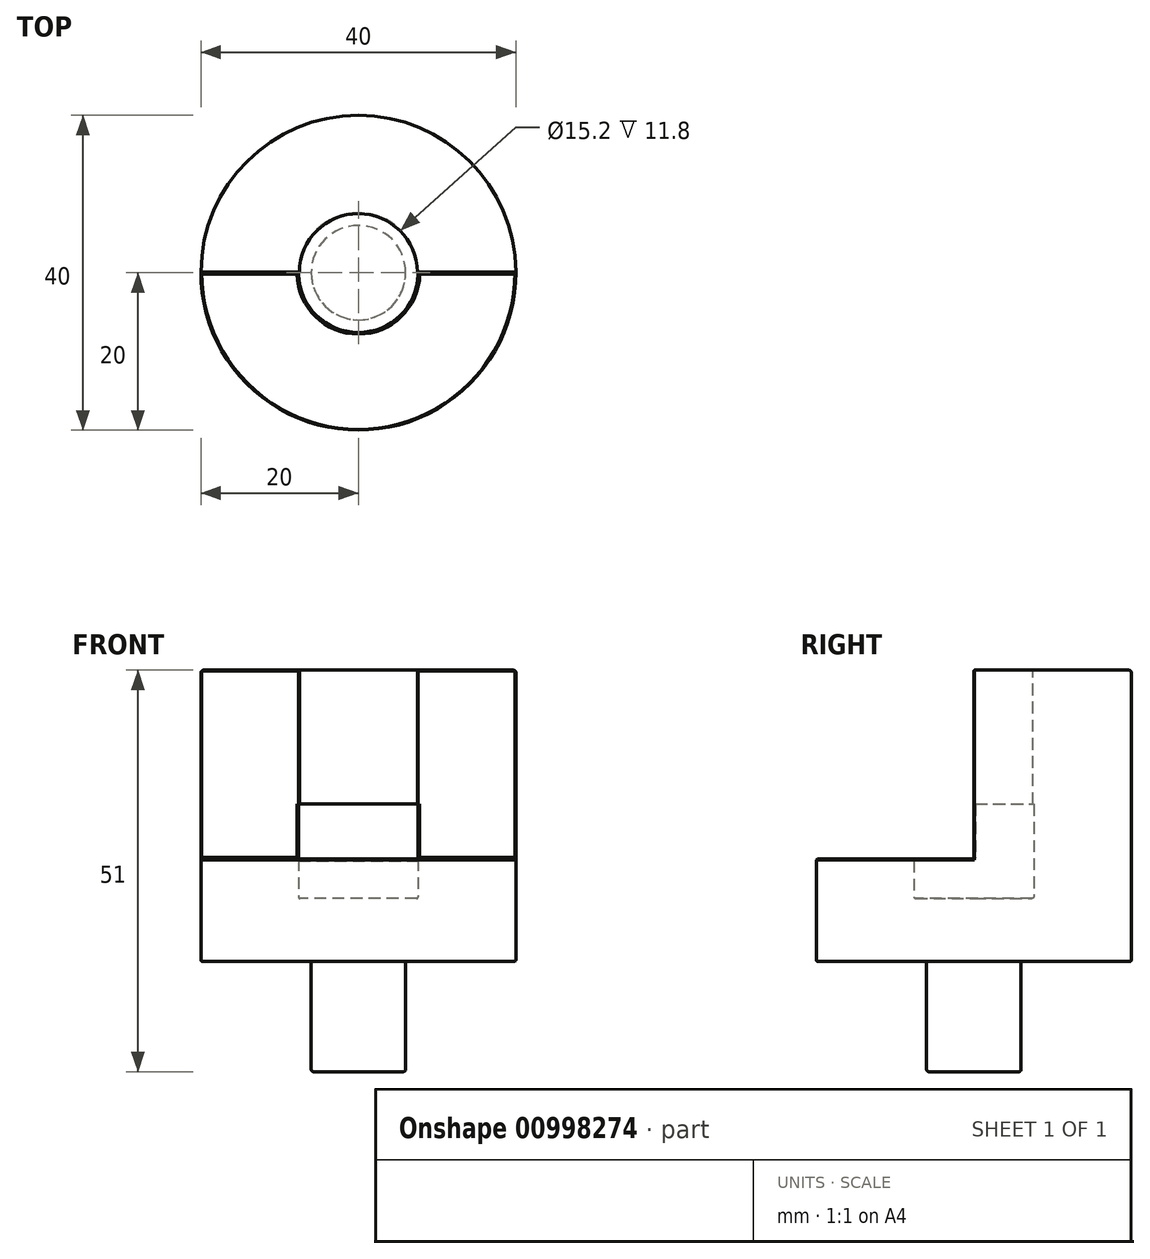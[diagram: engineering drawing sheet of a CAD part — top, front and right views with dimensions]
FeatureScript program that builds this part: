
annotation { "Feature Type Name" : "Feature", "Feature Type Description" : "" }
export const myFeature = defineFeature(function(context is Context, id is Id, definition is map)
    precondition{}
    {
        {
            var Q0;
            Q0=qCreatedBy(makeId("Top.planeOp"),FACE);
            var sketch = newSketch(context, id + "F0", { "sketchPlane" : qUnion([Q0])});
            skCircle(sketch, "E0", {"center": v(0, 0) * mm, "radius": 20 * mm});
            skSolve(sketch);
        }
        {
            var Q0;
            Q0 = qSketchRegion(id + "F0", true);
            extrude(context, id + "F1", {"entities" : qUnion([Q0]), "depth" : 37 * mm, "offsetDistance" : 25 * mm});
        }
        {
            var Q0;
            Q0=makeQuery(id+"F1.opExtrude","CAP_FACE",FACE,{"disambiguationData":[OSD([sQuery(id+"F0.wireOp",EDGE,"E0")])],"isStart":true});
            var sketch = newSketch(context, id + "F2", { "sketchPlane" : qUnion([Q0])});
            skCircle(sketch, "E1", {"center": v(0, 0) * mm, "radius": 6 * mm});
            skSolve(sketch);
        }
        {
            var Q0;
            Q0 = qSketchRegion(id + "F2", true);
            extrude(context, id + "F3", {"entities" : qUnion([Q0]), "operationType" : NewBodyOperationType.ADD, "depth" : 14 * mm, "offsetDistance" : 25 * mm});
        }
        {
            var Q0;
            Q0=makeQuery(id+"F1.opExtrude","CAP_FACE",FACE,{"disambiguationData":[OSD([sQuery(id+"F0.wireOp",EDGE,"E0")])],"isStart":false});
            var sketch = newSketch(context, id + "F4", { "sketchPlane" : qUnion([Q0])});
            skCircle(sketch, "E2", {"center": v(0, 0) * mm, "radius": 7.5 * mm});
            skSolve(sketch);
        }
        {
            var Q0;
            Q0=makeQuery(id+"F4.imprint","IMPRINT",FACE,{"disambiguationData":[TD([[makeQuery(id+"F4.imprint","IMPRINT",EDGE,{"derivedFrom":sQuery(id+"F4.wireOp",EDGE,"E2")}),1.0]])]});
            extrude(context, id + "F5", {"entities" : qUnion([Q0]), "operationType" : NewBodyOperationType.REMOVE, "oppositeDirection" : true, "depth" : 29 * mm, "offsetDistance" : 25 * mm});
        }
        {
            var Q0;
            Q0=qCreatedBy(makeId("Front.planeOp"),FACE);
            var sketch = newSketch(context, id + "F6", { "sketchPlane" : qUnion([Q0])});
            skLineSegment(sketch, "E3", {"start": v(-39.79, 13) * mm, "end": v(43.41, 13) * mm});
            skLineSegment(sketch, "E4", {"start": v(43.41, 13) * mm, "end": v(43.41, 53.9) * mm});
            skLineSegment(sketch, "E5", {"start": v(43.41, 53.9) * mm, "end": v(-42.56, 53.9) * mm});
            skLineSegment(sketch, "E6", {"start": v(-42.56, 53.9) * mm, "end": v(-39.79, 13) * mm});
            skSolve(sketch);
        }
        {
            var Q0;
            Q0=makeQuery(id+"F6.imprint","IMPRINT",FACE,{"disambiguationData":[TD([[makeQuery(id+"F6.imprint","IMPRINT",EDGE,{"derivedFrom":sQuery(id+"F6.wireOp",EDGE,"E3")}),1.0]])]});
            extrude(context, id + "F7", {"entities" : qUnion([Q0]), "operationType" : NewBodyOperationType.REMOVE, "oppositeDirection" : true, "depth" : -25 * mm, "offsetDistance" : 25 * mm});
        }
        {
            var Q0;
            Q0=makeQuery(id+"F5.boolean.opBoolean","COPY",FACE,{"derivedFrom":makeQuery(id+"F5.opExtrude","CAP_FACE",FACE,{"disambiguationData":[OSD([sQuery(id+"F4.wireOp",EDGE,"E2")])],"isStart":false})});
            var sketch = newSketch(context, id + "F8", { "sketchPlane" : qUnion([Q0])});
            skCircle(sketch, "E7", {"center": v(0, 0) * mm, "radius": 7.6 * mm});
            skSolve(sketch);
        }
        {
            var Q0;
            Q0 = qSketchRegion(id + "F8", true);
            extrude(context, id + "F9", {"entities" : qUnion([Q0]), "operationType" : NewBodyOperationType.REMOVE, "oppositeDirection" : true, "depth" : -12 * mm, "offsetDistance" : 25 * mm});
        }
        {
            var Q0;
            Q0=makeQuery(id+"F3.opExtrude","CAP_EDGE",EDGE,{"disambiguationData":[OSD([sQuery(id+"F2.wireOp",EDGE,"E1")])],"isStart":false});
            var Q1;
            Q1=makeQuery(id+"F1.opExtrude","CAP_EDGE",EDGE,{"disambiguationData":[OSD([sQuery(id+"F0.wireOp",EDGE,"E0")])],"isStart":false});
            fillet(context, id + "F10", {"entities" : qUnion([Q0, Q1]), "radius" : .3 * mm, "tangentPropagation" : true, "allowEdgeOverflow" : false});
        }
        {
            var Q0;
            Q0=makeQuery(id+"F7.boolean.opBoolean","INTERSECT",EDGE,{"disambiguationData":[OD(0.0)],"derivedFrom":[makeQuery(id+"F5.boolean.opBoolean","COPY",FACE,{"derivedFrom":makeQuery(id+"F5.opExtrude","SWEPT_FACE",FACE,{"disambiguationData":[OSD([sQuery(id+"F4.wireOp",EDGE,"E2")])]})}),makeQuery(id+"F7.opExtrude","CAP_FACE",FACE,{"disambiguationData":[OSD([sQuery(id+"F6.wireOp",EDGE,"E3"),sQuery(id+"F6.wireOp",EDGE,"E4"),sQuery(id+"F6.wireOp",EDGE,"E5"),sQuery(id+"F6.wireOp",EDGE,"E6")])],"isStart":true})]});
            var Q1;
            Q1=makeQuery(id+"F7.boolean.opBoolean","INTERSECT",EDGE,{"disambiguationData":[OD(1.0)],"derivedFrom":[makeQuery(id+"F5.boolean.opBoolean","COPY",FACE,{"derivedFrom":makeQuery(id+"F5.opExtrude","SWEPT_FACE",FACE,{"disambiguationData":[OSD([sQuery(id+"F4.wireOp",EDGE,"E2")])]})}),makeQuery(id+"F7.opExtrude","CAP_FACE",FACE,{"disambiguationData":[OSD([sQuery(id+"F6.wireOp",EDGE,"E3"),sQuery(id+"F6.wireOp",EDGE,"E4"),sQuery(id+"F6.wireOp",EDGE,"E5"),sQuery(id+"F6.wireOp",EDGE,"E6")])],"isStart":true})]});
            var Q2;
            Q2=makeQuery(id+"F5.boolean.opBoolean","COPY",EDGE,{"derivedFrom":makeQuery(id+"F5.opExtrude","CAP_EDGE",EDGE,{"disambiguationData":[OSD([sQuery(id+"F4.wireOp",EDGE,"E2")])],"isStart":true})});
            var Q3;
            Q3=makeQuery(id+"F7.boolean.opBoolean","INTERSECT",EDGE,{"disambiguationData":[OD(1.0)],"derivedFrom":[makeQuery(id+"F1.opExtrude","CAP_FACE",FACE,{"disambiguationData":[OSD([sQuery(id+"F0.wireOp",EDGE,"E0")])],"isStart":false}),makeQuery(id+"F7.opExtrude","CAP_FACE",FACE,{"disambiguationData":[OSD([sQuery(id+"F6.wireOp",EDGE,"E3"),sQuery(id+"F6.wireOp",EDGE,"E4"),sQuery(id+"F6.wireOp",EDGE,"E5"),sQuery(id+"F6.wireOp",EDGE,"E6")])],"isStart":true})]});
            var Q4;
            Q4=makeQuery(id+"F7.boolean.opBoolean","INTERSECT",EDGE,{"derivedFrom":[makeQuery(id+"F1.opExtrude","SWEPT_FACE",FACE,{"disambiguationData":[OSD([sQuery(id+"F0.wireOp",EDGE,"E0")])]}),makeQuery(id+"F7.opExtrude","SWEPT_FACE",FACE,{"disambiguationData":[OSD([sQuery(id+"F6.wireOp",EDGE,"E3")])]})]});
            var Q5;
            Q5=makeQuery(id+"F7.boolean.opBoolean","INTERSECT",EDGE,{"disambiguationData":[OD(0.0)],"derivedFrom":[makeQuery(id+"F1.opExtrude","CAP_FACE",FACE,{"disambiguationData":[OSD([sQuery(id+"F0.wireOp",EDGE,"E0")])],"isStart":false}),makeQuery(id+"F7.opExtrude","CAP_FACE",FACE,{"disambiguationData":[OSD([sQuery(id+"F6.wireOp",EDGE,"E3"),sQuery(id+"F6.wireOp",EDGE,"E4"),sQuery(id+"F6.wireOp",EDGE,"E5"),sQuery(id+"F6.wireOp",EDGE,"E6")])],"isStart":true})]});
            var Q6;
            Q6=makeQuery(id+"F7.boolean.opBoolean","INTERSECT",EDGE,{"disambiguationData":[OD(0.0)],"derivedFrom":[makeQuery(id+"F1.opExtrude","SWEPT_FACE",FACE,{"disambiguationData":[OSD([sQuery(id+"F0.wireOp",EDGE,"E0")])]}),makeQuery(id+"F7.opExtrude","CAP_FACE",FACE,{"disambiguationData":[OSD([sQuery(id+"F6.wireOp",EDGE,"E3"),sQuery(id+"F6.wireOp",EDGE,"E4"),sQuery(id+"F6.wireOp",EDGE,"E5"),sQuery(id+"F6.wireOp",EDGE,"E6")])],"isStart":true})]});
            var Q7;
            Q7=makeQuery(id+"F7.boolean.opBoolean","INTERSECT",EDGE,{"disambiguationData":[OD(1.0)],"derivedFrom":[makeQuery(id+"F1.opExtrude","SWEPT_FACE",FACE,{"disambiguationData":[OSD([sQuery(id+"F0.wireOp",EDGE,"E0")])]}),makeQuery(id+"F7.opExtrude","CAP_FACE",FACE,{"disambiguationData":[OSD([sQuery(id+"F6.wireOp",EDGE,"E3"),sQuery(id+"F6.wireOp",EDGE,"E4"),sQuery(id+"F6.wireOp",EDGE,"E5"),sQuery(id+"F6.wireOp",EDGE,"E6")])],"isStart":true})]});
            chamfer(context, id + "F11", {"entities" : qUnion([Q0, Q1, Q2, Q3, Q4, Q5, Q6, Q7]), "width" : .1 * mm, "tangentPropagation" : true});
        }
        {
            var Q0;
            Q0=makeQuery(id+"F7.boolean.opBoolean","COPY",EDGE,{"disambiguationData":[OD(0.0)],"derivedFrom":makeQuery(id+"F7.opExtrude","CAP_EDGE",EDGE,{"disambiguationData":[OSD([sQuery(id+"F6.wireOp",EDGE,"E3")])],"isStart":true})});
            var Q1;
            Q1=makeQuery(id+"F7.boolean.opBoolean","COPY",EDGE,{"disambiguationData":[OD(1.0)],"derivedFrom":makeQuery(id+"F7.opExtrude","CAP_EDGE",EDGE,{"disambiguationData":[OSD([sQuery(id+"F6.wireOp",EDGE,"E3")])],"isStart":true})});
            var Q2;
            Q2=makeQuery(id+"F9.boolean.opBoolean","INTERSECT",EDGE,{"derivedFrom":[makeQuery(id+"F7.boolean.opBoolean","COPY",FACE,{"derivedFrom":makeQuery(id+"F7.opExtrude","SWEPT_FACE",FACE,{"disambiguationData":[OSD([sQuery(id+"F6.wireOp",EDGE,"E3")])]})}),makeQuery(id+"F9.opExtrude","SWEPT_FACE",FACE,{"disambiguationData":[OSD([sQuery(id+"F8.wireOp",EDGE,"E7")])]})]});
            chamfer(context, id + "F12", {"entities" : qUnion([Q0, Q1, Q2]), "width" : .2 * mm, "tangentPropagation" : true});
        }
        {
            var Q0;
            Q0=makeQuery(id+"F9.boolean.opBoolean","COPY",EDGE,{"derivedFrom":makeQuery(id+"F9.opExtrude","CAP_EDGE",EDGE,{"disambiguationData":[OSD([sQuery(id+"F8.wireOp",EDGE,"E7")])],"isStart":true})});
            fillet(context, id + "F13", {"entities" : qUnion([Q0]), "radius" : .2 * mm, "tangentPropagation" : true, "allowEdgeOverflow" : false});
        }
        {
            var Q0;
            Q0=makeQuery(id+"F1.opExtrude","CAP_FACE",FACE,{"disambiguationData":[OSD([sQuery(id+"F0.wireOp",EDGE,"E0")])],"isStart":true});
            fillet(context, id + "F14", {"entities" : qUnion([Q0]), "radius" : .2 * mm, "tangentPropagation" : true, "allowEdgeOverflow" : false});
        }
    });
